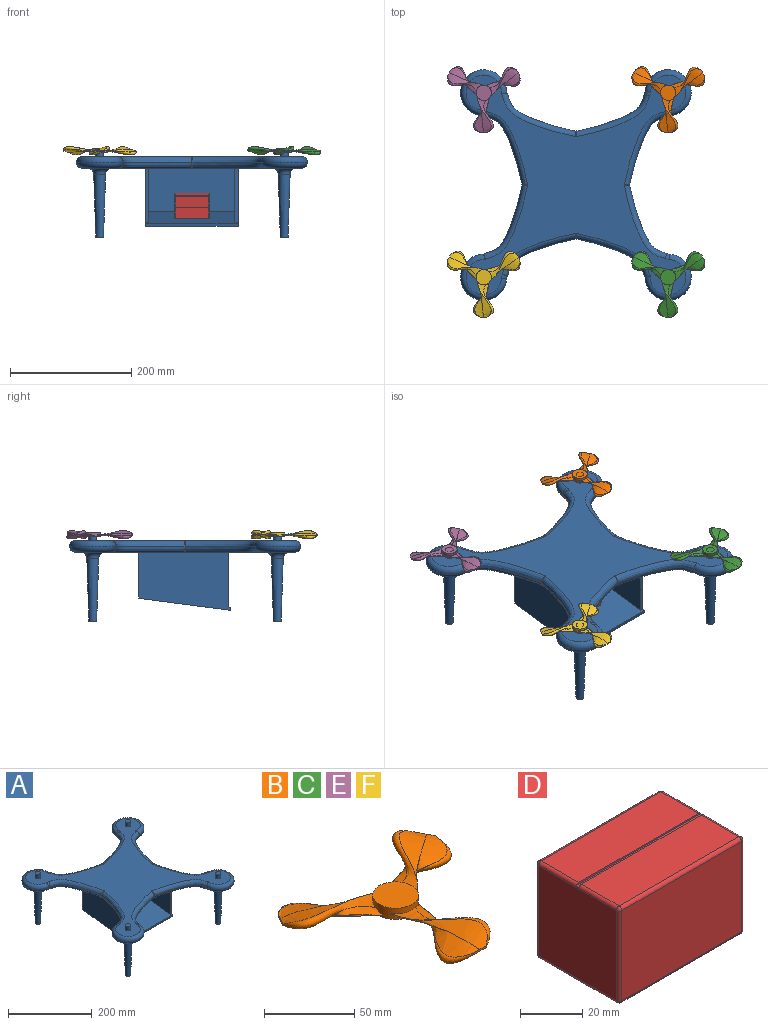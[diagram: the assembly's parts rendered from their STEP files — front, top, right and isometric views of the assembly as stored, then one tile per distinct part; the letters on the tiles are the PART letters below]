
ASSEMBLY  parts=6 mates=5
PART A: 90 faces, bbox 387.3x387.3x146.1 mm
  f0: torus R=80.01mm, axis (0,0,1), area 10mm2, adj f9,f50,f64
  f1: torus R=80.01mm, axis (0,0,1), area 10mm2, adj f9,f33,f47
  f2: torus R=80.01mm, axis (0,0,1), area 10mm2, adj f9,f16,f30
  f3: torus R=80.01mm, axis (0,0,1), area 10mm2, adj f10,f17,f31
  f4: torus R=80.01mm, axis (0,0,1), area 10mm2, adj f10,f14,f68
  f5: torus R=80.01mm, axis (0,0,1), area 10mm2, adj f10,f34,f48
  f6: extruded ~114.3x63.5mm, area 175.6mm2, adj f7,f11,f14,f63
  f7: cylinder r=38.1mm len=76.2mm, axis (0,0,-1), area 225.4mm2, adj f6,f15,f18,f21
  f8: extruded ~113.41x61.98mm, area 173.3mm2, adj f16,f17,f21,f27
  f9: plane 363.22x363.22mm, normal (0,0,1), area 48947.5mm2, adj f0,f1,f2,f11,f12,f15,f16,f19
  f10: plane 363.22x363.22mm, normal (0,0,-1), area 42215mm2, adj f3,f4,f5,f13,f14,f17,f18,f20
  f11: bspline ~126.83x75.81mm, area 1993.1mm2, adj f6,f9,f12,f15
  f12: torus R=80.01mm, axis (0,0,1), area 10mm2, adj f9,f11,f67
  f13: torus R=80.01mm, axis (0,0,1), area 10mm2, adj f10,f51,f65
  f14: bspline ~126.83x75.81mm, area 1993.1mm2, adj f4,f6,f10,f18
  f15: torus R=29.21mm, axis (0,0,1), area 2289.3mm2, adj f7,f9,f11,f19
  f16: bspline ~124.62x72.03mm, area 1953.8mm2, adj f2,f8,f9,f19
  f17: bspline ~124.62x72.03mm, area 1953.8mm2, adj f3,f8,f10,f20
  f18: torus R=29.21mm, axis (0,0,1), area 2289.3mm2, adj f7,f10,f14,f20
  f19: torus R=17.78mm, axis (0,0,1), area 70.3mm2, adj f9,f15,f16,f21
  f20: torus R=17.78mm, axis (0,0,1), area 70.3mm2, adj f10,f17,f18,f21
  f21: cylinder r=8.89mm len=3.54mm, axis (0,0,-1), area 4.7mm2, adj f7,f8,f19,f20
  f22: cylinder r=6.35mm len=12.7mm, axis (0,0,-1), area 506.7mm2, adj f9,f23
  f23: plane 12.7x12.7mm, normal (0,0,1), area 126.7mm2, adj f22
  f24: plane 12.7x12.7mm, normal (0,0,-1), area 126.7mm2, adj f25
  f25: cone r=10.16mm half-angle=1.9deg, axis (0,0,1), area 5314.6mm2, adj f24,f26
  f26: torus R=19.99mm, axis (0,0,1), area 1334.7mm2, adj f10,f25
  f27: extruded ~114.3x63.5mm, area 175.6mm2, adj f8,f28,f30,f31
  f28: cylinder r=38.1mm len=76.2mm, axis (0,0,-1), area 225.4mm2, adj f27,f32,f35,f38
  f29: extruded ~113.41x61.98mm, area 173.3mm2, adj f33,f34,f38,f44
  f30: bspline ~126.83x75.81mm, area 1993.1mm2, adj f2,f9,f27,f32
  f31: bspline ~126.83x75.81mm, area 1993.1mm2, adj f3,f10,f27,f35
  f32: torus R=29.21mm, axis (0,0,1), area 2289.3mm2, adj f9,f28,f30,f36
  f33: bspline ~124.62x72.03mm, area 1953.8mm2, adj f1,f9,f29,f36
  f34: bspline ~124.62x72.03mm, area 1953.8mm2, adj f5,f10,f29,f37
  f35: torus R=29.21mm, axis (0,0,1), area 2289.3mm2, adj f10,f28,f31,f37
  f36: torus R=17.78mm, axis (0,0,1), area 70.3mm2, adj f9,f32,f33,f38
  f37: torus R=17.78mm, axis (0,0,1), area 70.3mm2, adj f10,f34,f35,f38
  f38: cylinder r=8.89mm len=3.54mm, axis (0,0,-1), area 4.7mm2, adj f28,f29,f36,f37
  f39: cylinder r=6.35mm len=12.7mm, axis (0,0,-1), area 506.7mm2, adj f9,f40
  f40: plane 12.7x12.7mm, normal (0,0,1), area 126.7mm2, adj f39
  f41: plane 12.7x12.7mm, normal (0,0,-1), area 126.7mm2, adj f42
  f42: cone r=10.16mm half-angle=1.9deg, axis (0,0,1), area 5314.6mm2, adj f41,f43
  f43: torus R=19.99mm, axis (0,0,1), area 1334.7mm2, adj f10,f42
  f44: extruded ~114.3x63.5mm, area 175.6mm2, adj f29,f45,f47,f48
  f45: cylinder r=38.1mm len=76.2mm, axis (0,0,-1), area 225.4mm2, adj f44,f49,f52,f55
  f46: extruded ~113.41x61.98mm, area 173.3mm2, adj f50,f51,f55,f61
  f47: bspline ~126.83x75.81mm, area 1993.1mm2, adj f1,f9,f44,f49
  f48: bspline ~126.83x75.81mm, area 1993.1mm2, adj f5,f10,f44,f52
  f49: torus R=29.21mm, axis (0,0,1), area 2289.3mm2, adj f9,f45,f47,f53
  f50: bspline ~124.62x72.03mm, area 1953.8mm2, adj f0,f9,f46,f53
  f51: bspline ~124.62x72.03mm, area 1953.8mm2, adj f10,f13,f46,f54
  f52: torus R=29.21mm, axis (0,0,1), area 2289.3mm2, adj f10,f45,f48,f54
  f53: torus R=17.78mm, axis (0,0,1), area 70.3mm2, adj f9,f49,f50,f55
  f54: torus R=17.78mm, axis (0,0,1), area 70.3mm2, adj f10,f51,f52,f55
  f55: cylinder r=8.89mm len=3.54mm, axis (0,0,-1), area 4.7mm2, adj f45,f46,f53,f54
  f56: cylinder r=6.35mm len=12.7mm, axis (0,0,-1), area 506.7mm2, adj f9,f57
  f57: plane 12.7x12.7mm, normal (0,0,1), area 126.7mm2, adj f56
  f58: plane 12.7x12.7mm, normal (0,0,-1), area 126.7mm2, adj f59
  f59: cone r=10.16mm half-angle=1.9deg, axis (0,0,1), area 5314.6mm2, adj f58,f60
  f60: torus R=19.99mm, axis (0,0,1), area 1334.7mm2, adj f10,f59
  f61: extruded ~114.3x63.5mm, area 175.6mm2, adj f46,f62,f64,f65
  f62: cylinder r=38.1mm len=76.2mm, axis (0,0,-1), area 225.4mm2, adj f61,f66,f69,f72
  f63: extruded ~113.41x61.98mm, area 173.3mm2, adj f6,f67,f68,f72
  f64: bspline ~126.83x75.81mm, area 1993.1mm2, adj f0,f9,f61,f66
  f65: bspline ~126.83x75.81mm, area 1993.1mm2, adj f10,f13,f61,f69
  f66: torus R=29.21mm, axis (0,0,1), area 2289.3mm2, adj f9,f62,f64,f70
  f67: bspline ~124.62x72.03mm, area 1953.8mm2, adj f9,f12,f63,f70
  f68: bspline ~124.62x72.03mm, area 1953.8mm2, adj f4,f10,f63,f71
  f69: torus R=29.21mm, axis (0,0,1), area 2289.3mm2, adj f10,f62,f65,f71
  f70: torus R=17.78mm, axis (0,0,1), area 70.3mm2, adj f9,f66,f67,f72
  f71: torus R=17.78mm, axis (0,0,1), area 70.3mm2, adj f10,f68,f69,f72
  f72: cylinder r=8.89mm len=3.54mm, axis (0,0,-1), area 4.7mm2, adj f62,f63,f70,f71
  f73: cylinder r=6.35mm len=12.7mm, axis (0,0,-1), area 506.7mm2, adj f9,f74
  f74: plane 12.7x12.7mm, normal (0,0,1), area 126.7mm2, adj f73
  f75: plane 12.7x12.7mm, normal (0,0,-1), area 126.7mm2, adj f76
  f76: cone r=10.16mm half-angle=1.9deg, axis (0,0,1), area 5314.6mm2, adj f75,f77
  f77: torus R=19.99mm, axis (0,0,1), area 1334.7mm2, adj f10,f76
  f78: plane 90.47x5.08mm, normal (0,-1,0), area 459.6mm2, adj f10,f79,f85,f89
  f79: plane 142.24x90.47mm, normal (1,0,0), area 11536.8mm2, adj f10,f78,f80,f89
  f80: plane 142.24x71.75mm, normal (0,-1,0), area 10205mm2, adj f10,f79,f81,f89
  f81: plane 142.24x90.47mm, normal (-1,0,0), area 11536.8mm2, adj f10,f80,f82,f89
  f82: plane 90.47x5.08mm, normal (0,-1,0), area 459.6mm2, adj f10,f81,f83,f89
  f83: plane 151.76x96.04mm, normal (1,0,0), area 12674mm2, adj f10,f82,f84,f86,f87,f88,f89
  f84: plane 152.4x72.84mm, normal (0,1,0), area 11101.5mm2, adj f10,f83,f85,f87
  f85: plane 151.76x96.04mm, normal (-1,0,0), area 12674mm2, adj f10,f78,f84,f86,f87,f88,f89
  f86: plane 152.4x151.1mm, normal (0,0.13,-0.99), area 23225.8mm2, adj f83,f85,f87,f88
  f87: plane 152.4x3.3mm, normal (0,0.99,0.13), area 507mm2, adj f83,f84,f85,f86
  f88: plane 152.4x5.04mm, normal (0,-0.99,-0.13), area 774.2mm2, adj f83,f85,f86,f89
  f89: plane 152.4x146.25mm, normal (0,-0.13,0.99), area 21022.4mm2, adj f78,f79,f80,f81,f82,f83,f85,f88
PART B: 26 faces, bbox 121.3x119.8x23.7 mm
  f0: cylinder r=12.7mm len=25.4mm, axis (0,0,-1), area 508.7mm2, adj f1,f2,f3,f4,f5,f6,f7,f8
  f1: plane 25.4x25.4mm, normal (0,0,1), area 506.7mm2, adj f0
  f2: plane 25.4x25.4mm, normal (0,0,-1), area 380mm2, adj f0,f24
  f3: bspline ~66.04x33.75mm, area 448.1mm2, adj f0,f4,f8,f9
  f4: bspline ~66.04x43.38mm, area 388.8mm2, adj f0,f3,f5,f9
  f5: bspline ~66.04x36.02mm, area 390.6mm2, adj f0,f4,f6,f9
  f6: bspline ~66.04x33.75mm, area 415.2mm2, adj f0,f5,f7,f9
  f7: bspline ~66.04x40.01mm, area 416.2mm2, adj f0,f6,f8,f9
  f8: bspline ~66.04x32.6mm, area 423.2mm2, adj f0,f3,f7,f9
  f9: plane 10.16x1.27mm, normal (0,-1,0), area 12.9mm2, adj f3,f4,f5,f6,f7,f8
  f10: plane 8.8x5.08mm, normal (-0.87,0.5,0), area 12.9mm2, adj f11,f12,f13,f14,f15,f16
  f11: bspline ~66.98x38.52mm, area 416.2mm2, adj f0,f10,f12,f16
  f12: bspline ~54.02x42.92mm, area 415.2mm2, adj f0,f10,f11,f13
  f13: bspline ~46.48x43.78mm, area 390.6mm2, adj f0,f10,f12,f14
  f14: bspline ~57.06x56.56mm, area 388.8mm2, adj f0,f10,f13,f15
  f15: bspline ~53.52x36.23mm, area 448.1mm2, adj f0,f10,f14,f16
  f16: bspline ~58.81x21.4mm, area 423.2mm2, adj f0,f10,f11,f15
  f17: bspline ~51.56x35.92mm, area 448.2mm2, adj f0,f18,f22,f23
  f18: bspline ~53.94x23.05mm, area 388.8mm2, adj f0,f17,f19,f23
  f19: bspline ~65.45x29.72mm, area 390.6mm2, adj f0,f18,f20,f23
  f20: bspline ~54.16x31.47mm, area 415.2mm2, adj f0,f19,f21,f23
  f21: bspline ~61.77x60.37mm, area 416.2mm2, adj f0,f20,f22,f23
  f22: bspline ~46.36x45.1mm, area 423.2mm2, adj f0,f17,f21,f23
  f23: plane 8.8x5.08mm, normal (0.87,0.5,0), area 12.9mm2, adj f17,f18,f19,f20,f21,f22
  f24: cylinder r=6.35mm len=12.7mm, axis (0,0,-1), area 253.4mm2, adj f2,f25
  f25: plane 12.7x12.7mm, normal (0,0,-1), area 126.7mm2, adj f24
PART C: same geometry as B
PART D: 34 faces, bbox 57.2x38.1x38.1 mm
  f0: plane 54.61x17.15mm, normal (0,0,-1), area 936.3mm2, adj f14,f15,f24,f31
  f1: plane 54.61x17.15mm, normal (0,0,1), area 936.3mm2, adj f11,f12,f21,f29
  f2: plane 35.56x35.56mm, normal (1,0,0), area 1264.5mm2, adj f16,f21,f24,f27
  f3: plane 54.61x35.56mm, normal (0,1,0), area 1941.9mm2, adj f13,f22,f23,f27
  f4: plane 35.56x35.56mm, normal (-1,0,0), area 1264.5mm2, adj f8,f12,f13,f14
  f5: plane 54.61x35.56mm, normal (0,-1,0), area 1941.9mm2, adj f8,f11,f15,f16
  f6: plane 54.61x17.15mm, normal (0,0,1), area 936.3mm2, adj f12,f21,f22,f28
  f7: plane 54.61x17.15mm, normal (0,0,-1), area 936.3mm2, adj f14,f23,f24,f32
  f8: cylinder r=1.27mm len=35.56mm, axis (0,0,1), area 70.9mm2, adj f4,f5,f9,f10
  f9: sphere r=1.27mm, area 2.5mm2, adj f8,f11,f12
  f10: sphere r=1.27mm, area 2.5mm2, adj f8,f14,f15
  f11: cylinder r=1.27mm len=54.61mm, axis (-1,0,0), area 108.9mm2, adj f1,f5,f9,f17
  f12: cylinder r=1.27mm len=35.56mm, axis (0,1,0), area 69.3mm2, adj f1,f4,f6,f9,f18,f28,f29,f30
  f13: cylinder r=1.27mm len=35.56mm, axis (0,0,-1), area 70.9mm2, adj f3,f4,f18,f19
  f14: cylinder r=1.27mm len=35.56mm, axis (0,-1,0), area 69.9mm2, adj f0,f4,f7,f10,f19,f31,f32,f33
  f15: cylinder r=1.27mm len=54.61mm, axis (1,0,0), area 108.9mm2, adj f0,f5,f10,f20
  f16: cylinder r=1.27mm len=35.56mm, axis (0,0,-1), area 70.9mm2, adj f2,f5,f17,f20
  f17: sphere r=1.27mm, area 2.5mm2, adj f11,f16,f21
  f18: sphere r=1.27mm, area 2.5mm2, adj f12,f13,f22
  f19: sphere r=1.27mm, area 2.5mm2, adj f13,f14,f23
  f20: sphere r=1.27mm, area 2.5mm2, adj f15,f16,f24
  f21: cylinder r=1.27mm len=35.56mm, axis (0,-1,0), area 69.3mm2, adj f1,f2,f6,f17,f25,f28,f29,f30
  f22: cylinder r=1.27mm len=54.61mm, axis (1,0,0), area 108.9mm2, adj f3,f6,f18,f25
  f23: cylinder r=1.27mm len=54.61mm, axis (-1,0,0), area 108.9mm2, adj f3,f7,f19,f26
  f24: cylinder r=1.27mm len=35.56mm, axis (0,1,0), area 69.9mm2, adj f0,f2,f7,f20,f26,f31,f32,f33
  f25: sphere r=1.27mm, area 2.5mm2, adj f21,f22,f27
  f26: sphere r=1.27mm, area 2.5mm2, adj f23,f24,f27
  f27: cylinder r=1.27mm len=35.56mm, axis (0,0,1), area 70.9mm2, adj f2,f3,f25,f26
  f28: plane 56.81x0.64mm, normal (0,-1,0), area 35.7mm2, adj f6,f12,f21,f30
  f29: plane 56.81x0.64mm, normal (0,1,0), area 35.7mm2, adj f1,f12,f21,f30
  f30: plane 56.81x1.27mm, normal (0,0,1), area 72.1mm2, adj f12,f21,f28,f29
  f31: plane 56.13x0.25mm, normal (0,1,0), area 14.1mm2, adj f0,f14,f24,f33
  f32: plane 56.13x0.25mm, normal (0,-1,0), area 14.1mm2, adj f7,f14,f24,f33
  f33: plane 56.13x1.27mm, normal (0,0,-1), area 71.3mm2, adj f14,f24,f31,f32
PART E: same geometry as B
PART F: same geometry as B
PLACE A t=(-94.53,-53.68,46.66)mm fixed
PLACE B t=(57.87,98.72,72.06)mm
PLACE C t=(57.87,-206.08,72.06)mm
PLACE D rot(axis=(1,0,0),97.5deg) t=(-94.53,-39.43,-13.36)mm
PLACE E t=(-246.93,98.72,72.06)mm
PLACE F t=(-246.93,-206.08,72.06)mm
MATE revolute E.f24 <-> A.f7  axis (0,0,-1) through (-246.93,98.72,78.41)mm
MATE revolute B.f24 <-> A.f62  axis (0,0,-1) through (57.87,98.72,78.41)mm
MATE revolute C.f24 <-> A.f45  axis (0,0,-1) through (57.87,-206.08,78.41)mm
MATE revolute F.f24 <-> A.f28  axis (0,0,-1) through (-246.93,-206.08,78.41)mm
MATE planar D.f5 <-> A.f89  axis (0,0.13,-0.99) through (-94.53,-55.83,-34.73)mm
